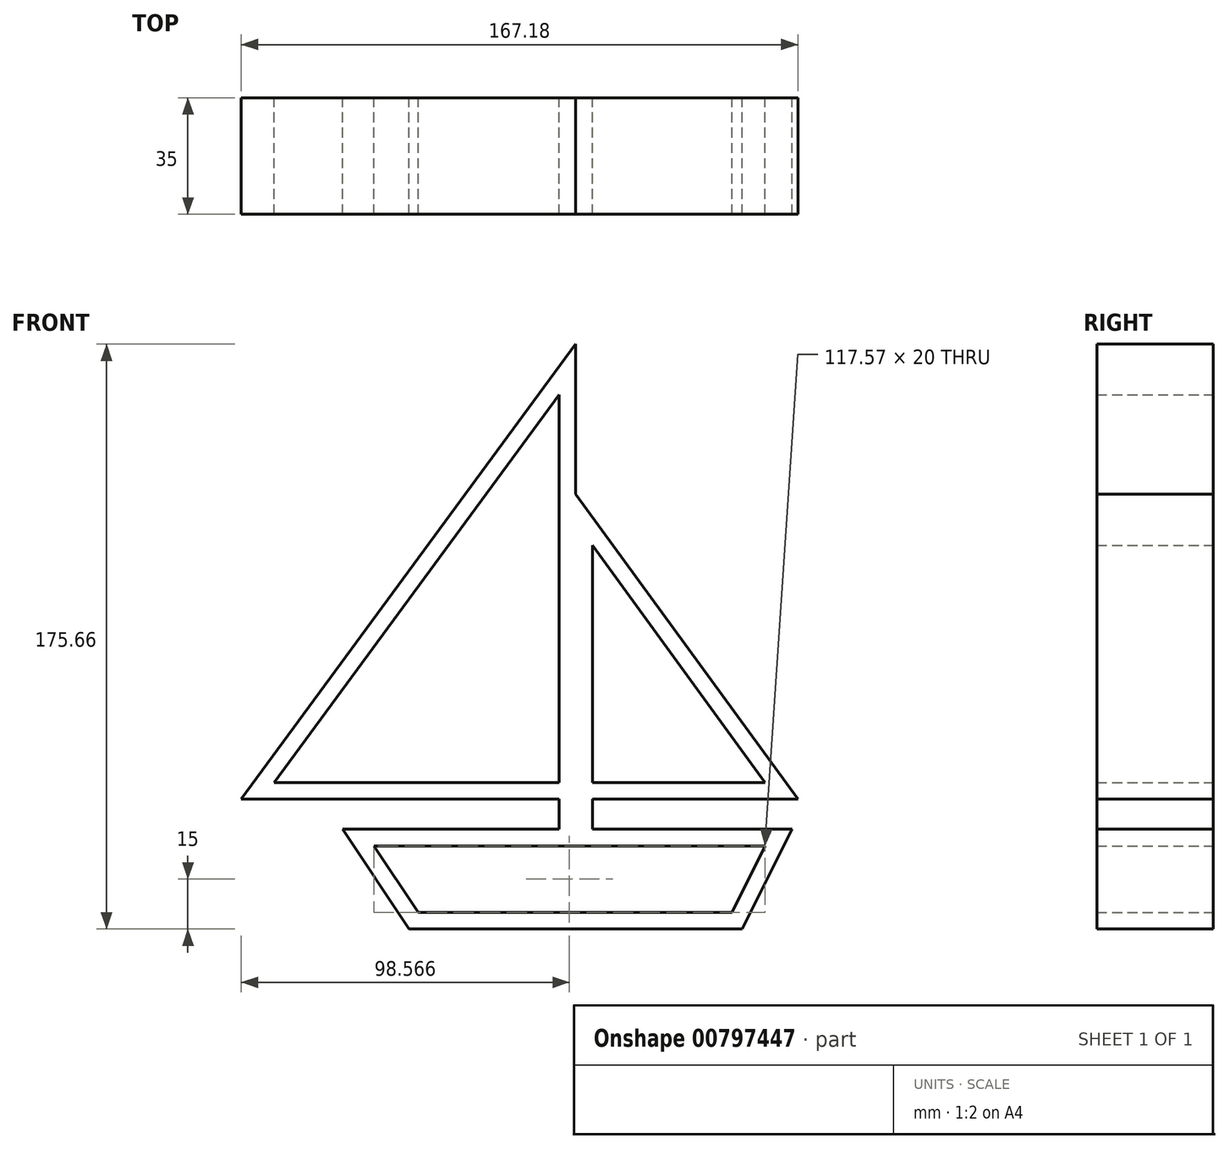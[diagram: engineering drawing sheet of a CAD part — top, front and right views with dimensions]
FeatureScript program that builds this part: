
annotation { "Feature Type Name" : "Feature", "Feature Type Description" : "" }
export const myFeature = defineFeature(function(context is Context, id is Id, definition is map)
    precondition{}
    {
        {
            var Q0;
            Q0=qCreatedBy(makeId("Front.planeOp"),FACE);
            var sketch = newSketch(context, id + "F0", { "sketchPlane" : qUnion([Q0])});
            skLineSegment(sketch, "E0", {"start": v(-50, -30) * mm, "end": v(50, -30) * mm});
            skLineSegment(sketch, "E1", {"start": v(-50, -30) * mm, "end": v(-70, 0) * mm});
            skLineSegment(sketch, "E2", {"start": v(65, 0) * mm, "end": v(50, -30) * mm});
            skLineSegment(sketch, "E3", {"start": v(0, 145.66) * mm, "end": v(-100.44, 9) * mm});
            skLineSegment(sketch, "E4", {"start": v(66.74, 9) * mm, "end": v(0, 100.56) * mm});
            skLineSegment(sketch, "E5", {"start": v(0, 145.66) * mm, "end": v(0, 100.56) * mm});
            skLineSegment(sketch, "E6", {"start": v(-60.66, -5) * mm, "end": v(56.9, -5) * mm});
            skLineSegment(sketch, "E7", {"start": v(56.9, -5) * mm, "end": v(46.9, -25) * mm});
            skLineSegment(sketch, "E8", {"start": v(46.9, -25) * mm, "end": v(-47.32, -25) * mm});
            skLineSegment(sketch, "E9", {"start": v(-47.32, -25) * mm, "end": v(-60.66, -5) * mm});
            skLineSegment(sketch, "E10", {"start": v(-5, 130.41) * mm, "end": v(-90.56, 14) * mm});
            skLineSegment(sketch, "E11", {"start": v(-90.56, 14) * mm, "end": v(-5, 14) * mm});
            skLineSegment(sketch, "E12", {"start": v(-5, 14) * mm, "end": v(-5, 130.41) * mm});
            skLineSegment(sketch, "E13", {"start": v(5, 85.21) * mm, "end": v(5, 14) * mm});
            skLineSegment(sketch, "E14", {"start": v(5, 14) * mm, "end": v(56.9, 14) * mm});
            skLineSegment(sketch, "E15", {"start": v(56.9, 14) * mm, "end": v(5, 85.21) * mm});
            skLineSegment(sketch, "E16", {"start": v(-70, 0) * mm, "end": v(65, 0) * mm});
            skLineSegment(sketch, "E17", {"start": v(-5, 14) * mm, "end": v(-5, 0) * mm});
            skLineSegment(sketch, "E18", {"start": v(5, 14) * mm, "end": v(5, 0) * mm});
            skLineSegment(sketch, "E19", {"start": v(-100.44, 9) * mm, "end": v(-5, 9) * mm});
            skLineSegment(sketch, "E20", {"start": v(66.74, 9) * mm, "end": v(5, 9) * mm});
            skLineSegment(sketch, "E21", {"start": v(0, 145.66) * mm, "end": v(0, 0) * mm});
            skSolve(sketch);
        }
        {
            var Q0;
            Q0 = qSketchRegion(id + "F0", true);
            extrude(context, id + "F1", {"entities" : qUnion([Q0]), "endBound" : BoundingType.SYMMETRIC, "depth" : 35 * mm, "offsetDistance" : 25 * mm});
        }
    });
